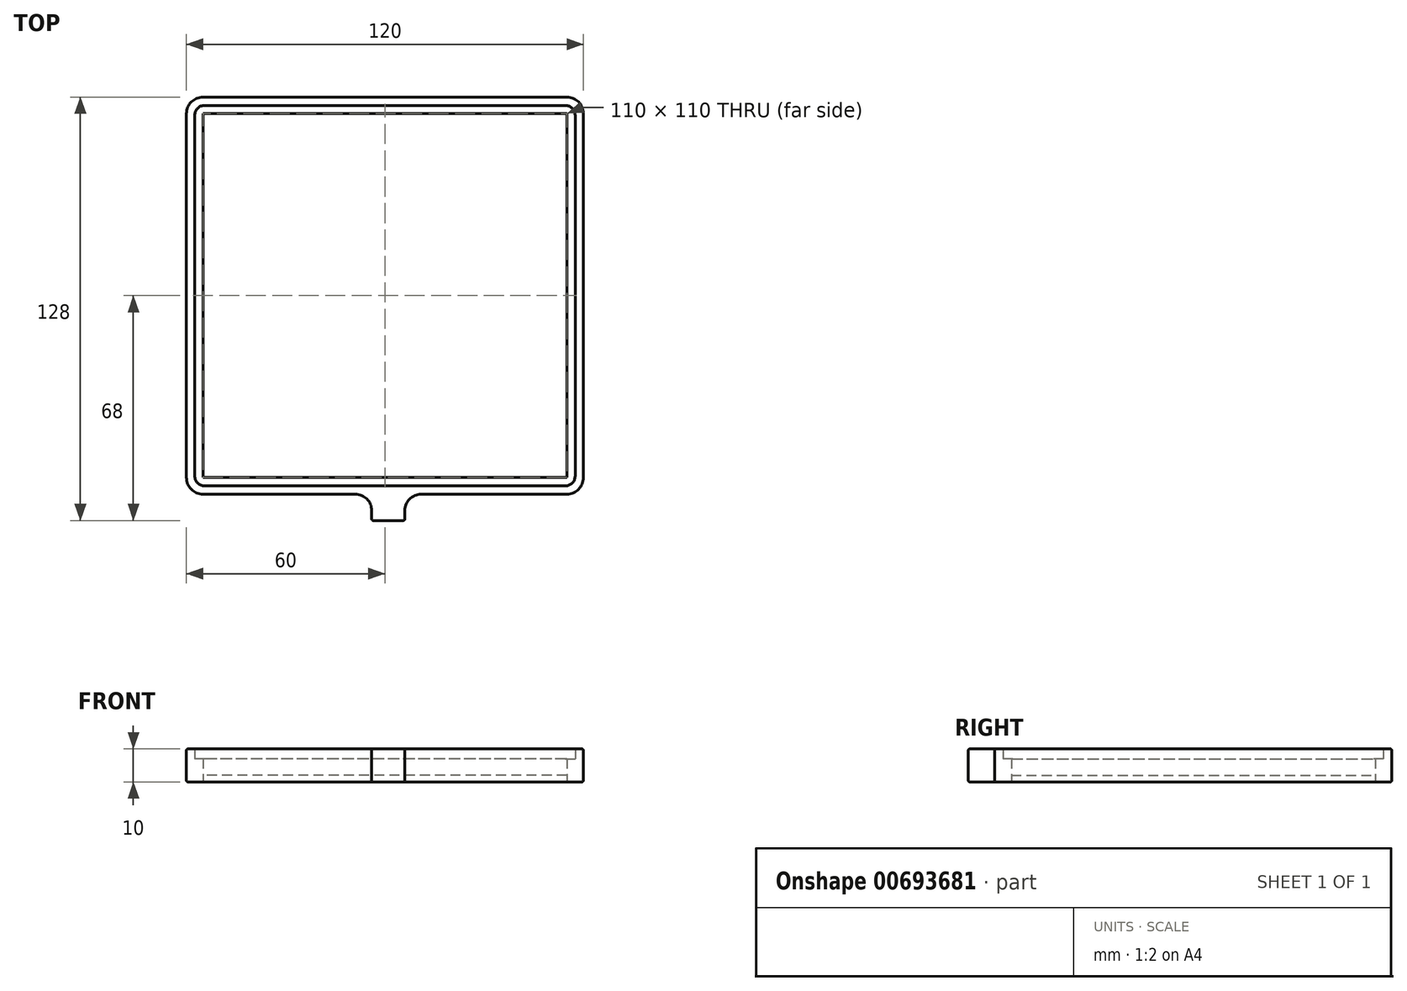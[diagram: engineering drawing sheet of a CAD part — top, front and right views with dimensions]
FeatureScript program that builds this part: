
annotation { "Feature Type Name" : "Feature", "Feature Type Description" : "" }
export const myFeature = defineFeature(function(context is Context, id is Id, definition is map)
    precondition{}
    {
        {
            var Q0;
            Q0=qCreatedBy(makeId("Top.planeOp"),FACE);
            var sketch = newSketch(context, id + "F0", { "sketchPlane" : qUnion([Q0])});
            skLineSegment(sketch, "E0.bottom", {"start": v(55, -55) * mm, "end": v(-55, -55) * mm});
            skLineSegment(sketch, "E0.top", {"start": v(55, 55) * mm, "end": v(-55, 55) * mm});
            skLineSegment(sketch, "E0.left", {"start": v(55, -55) * mm, "end": v(55, 55) * mm});
            skLineSegment(sketch, "E0.right", {"start": v(-55, -55) * mm, "end": v(-55, 55) * mm});
            skPoint(sketch, "E0.middle", {"position": v(0, 0) * mm});
            skLineSegment(sketch, "E1.bottom", {"start": v(55, -60) * mm, "end": v(-55, -60) * mm});
            skLineSegment(sketch, "E1.top", {"start": v(55, 60) * mm, "end": v(-55, 60) * mm});
            skLineSegment(sketch, "E1.left", {"start": v(60, -55) * mm, "end": v(60, 55) * mm});
            skLineSegment(sketch, "E1.right", {"start": v(-60, -55) * mm, "end": v(-60, 55) * mm});
            skPoint(sketch, "E2.visualSharp", {"position": v(-60, 60) * mm});
            skArc(sketch, "E2.filletArc", {"start": v(-55, 60) * mm, "mid": v(-58.54, 58.54) * mm, "end": v(-60, 55) * mm});
            skPoint(sketch, "E3.visualSharp", {"position": v(60, 60) * mm});
            skArc(sketch, "E3.filletArc", {"start": v(60, 55) * mm, "mid": v(58.54, 58.54) * mm, "end": v(55, 60) * mm});
            skPoint(sketch, "E4.visualSharp", {"position": v(-60, -60) * mm});
            skArc(sketch, "E4.filletArc", {"start": v(-60, -55) * mm, "mid": v(-58.54, -58.54) * mm, "end": v(-55, -60) * mm});
            skPoint(sketch, "E5.visualSharp", {"position": v(60, -60) * mm});
            skArc(sketch, "E5.filletArc", {"start": v(55, -60) * mm, "mid": v(58.54, -58.54) * mm, "end": v(60, -55) * mm});
            skLineSegment(sketch, "E6.bottom", {"start": v(54.5, -57.5) * mm, "end": v(-54.5, -57.5) * mm});
            skLineSegment(sketch, "E6.top", {"start": v(54.5, 57.5) * mm, "end": v(-54.5, 57.5) * mm});
            skLineSegment(sketch, "E6.left", {"start": v(57.5, -54.5) * mm, "end": v(57.5, 54.5) * mm});
            skLineSegment(sketch, "E6.right", {"start": v(-57.5, -54.5) * mm, "end": v(-57.5, 54.5) * mm});
            skPoint(sketch, "E7.visualSharp", {"position": v(-57.5, 57.5) * mm});
            skArc(sketch, "E7.filletArc", {"start": v(-54.5, 57.5) * mm, "mid": v(-56.62, 56.62) * mm, "end": v(-57.5, 54.5) * mm});
            skPoint(sketch, "E8.visualSharp", {"position": v(57.5, 57.5) * mm});
            skArc(sketch, "E8.filletArc", {"start": v(57.5, 54.5) * mm, "mid": v(56.62, 56.62) * mm, "end": v(54.5, 57.5) * mm});
            skPoint(sketch, "E9.visualSharp", {"position": v(-57.5, -57.5) * mm});
            skArc(sketch, "E9.filletArc", {"start": v(-57.5, -54.5) * mm, "mid": v(-56.62, -56.62) * mm, "end": v(-54.5, -57.5) * mm});
            skPoint(sketch, "E10.visualSharp", {"position": v(57.5, -57.5) * mm});
            skArc(sketch, "E10.filletArc", {"start": v(54.5, -57.5) * mm, "mid": v(56.62, -56.62) * mm, "end": v(57.5, -54.5) * mm});
            skLineSegment(sketch, "E11.bottom", {"start": v(6, -68) * mm, "end": v(-4, -68) * mm});
            skLineSegment(sketch, "E11.top", {"start": v(6, -60) * mm, "end": v(-4, -60) * mm});
            skLineSegment(sketch, "E11.left", {"start": v(6, -68) * mm, "end": v(6, -60) * mm});
            skLineSegment(sketch, "E11.right", {"start": v(-4, -68) * mm, "end": v(-4, -60) * mm});
            skPoint(sketch, "E11.middle", {"position": v(1, -64) * mm});
            skSolve(sketch);
        }
        {
            var Q0;
            Q0=makeQuery(id+"F0.imprint","IMPRINT",FACE,{"disambiguationData":[TD([[makeQuery(id+"F0.imprint","IMPRINT",EDGE,{"derivedFrom":sQuery(id+"F0.wireOp",EDGE,"E0.bottom")}),-1.0]])]});
            extrude(context, id + "F1", {"entities" : qUnion([Q0]), "depth" : 2 * mm, "offsetDistance" : 25 * mm});
        }
        {
            var Q0;
            Q0=makeQuery(id+"F0.imprint","IMPRINT",FACE,{"disambiguationData":[TD([[makeQuery(id+"F0.imprint","IMPRINT",EDGE,{"derivedFrom":sQuery(id+"F0.wireOp",EDGE,"E0.bottom")}),1.0]])]});
            extrude(context, id + "F2", {"entities" : qUnion([Q0]), "depth" : 7 * mm, "offsetDistance" : 25 * mm});
        }
        {
            var Q0;
            Q0 = qSketchRegion(id + "F0", true);
            extrude(context, id + "F3", {"entities" : qUnion([Q0]), "operationType" : NewBodyOperationType.ADD, "depth" : 10 * mm, "offsetDistance" : 25 * mm});
        }
        {
            var Q0;
            Q0=makeQuery(id+"F3.opExtrude","SWEPT_EDGE",EDGE,{"disambiguationData":[OSD([sQuery(id+"F0.wireOp",EDGE,"E1.bottom"),sQuery(id+"F0.wireOp",EDGE,"E11.top"),sQuery(id+"F0.wireOp",EDGE,"E11.left")])]});
            var Q1;
            Q1=makeQuery(id+"F3.opExtrude","SWEPT_EDGE",EDGE,{"disambiguationData":[OSD([sQuery(id+"F0.wireOp",EDGE,"E1.bottom"),sQuery(id+"F0.wireOp",EDGE,"E11.top"),sQuery(id+"F0.wireOp",EDGE,"E11.right")])]});
            fillet(context, id + "F4", {"entities" : qUnion([Q0, Q1]), "radius" : 5 * mm, "tangentPropagation" : true, "allowEdgeOverflow" : false});
        }
        {
            var Q0;
            Q0=makeQuery(id+"F3.opExtrude","SWEPT_EDGE",EDGE,{"disambiguationData":[OSD([sQuery(id+"F0.wireOp",EDGE,"E11.bottom"),sQuery(id+"F0.wireOp",EDGE,"E11.left")])]});
            var Q1;
            Q1=makeQuery(id+"F3.opExtrude","CAP_EDGE",EDGE,{"disambiguationData":[OSD([sQuery(id+"F0.wireOp",EDGE,"E11.bottom")])],"isStart":false});
            var Q2;
            Q2=makeQuery(id+"F3.opExtrude","SWEPT_EDGE",EDGE,{"disambiguationData":[OSD([sQuery(id+"F0.wireOp",EDGE,"E11.bottom"),sQuery(id+"F0.wireOp",EDGE,"E11.right")])]});
            var Q3;
            Q3=makeQuery(id+"F3.opExtrude","CAP_EDGE",EDGE,{"disambiguationData":[OSD([sQuery(id+"F0.wireOp",EDGE,"E11.bottom")])],"isStart":true});
            var Q4;
            {var subQ0=sQuery(id+"F0.wireOp",EDGE,"E1.bottom");Q4=makeQuery(id+"F3.opExtrude","CAP_EDGE",EDGE,{"disambiguationData":[OSD([subQ0]),TDD([makeQuery(id+"F0.imprint","IMPRINT",EDGE,{"disambiguationData":[TD([[makeQuery(id+"F0.imprint","INTERSECT",VERTEX,{"derivedFrom":[subQ0,sQuery(id+"F0.wireOp",EDGE,"E5.filletArc")]}),-1.0]])],"derivedFrom":subQ0})])],"isStart":false});}
            var Q5;
            Q5=makeQuery(id+"F3.opExtrude","CAP_EDGE",EDGE,{"disambiguationData":[OSD([sQuery(id+"F0.wireOp",EDGE,"E1.left")])],"isStart":true});
            fillet(context, id + "F5", {"entities" : qUnion([Q0, Q1, Q2, Q3, Q4, Q5]), "radius" : .5 * mm, "tangentPropagation" : true, "allowEdgeOverflow" : false});
        }
    });
